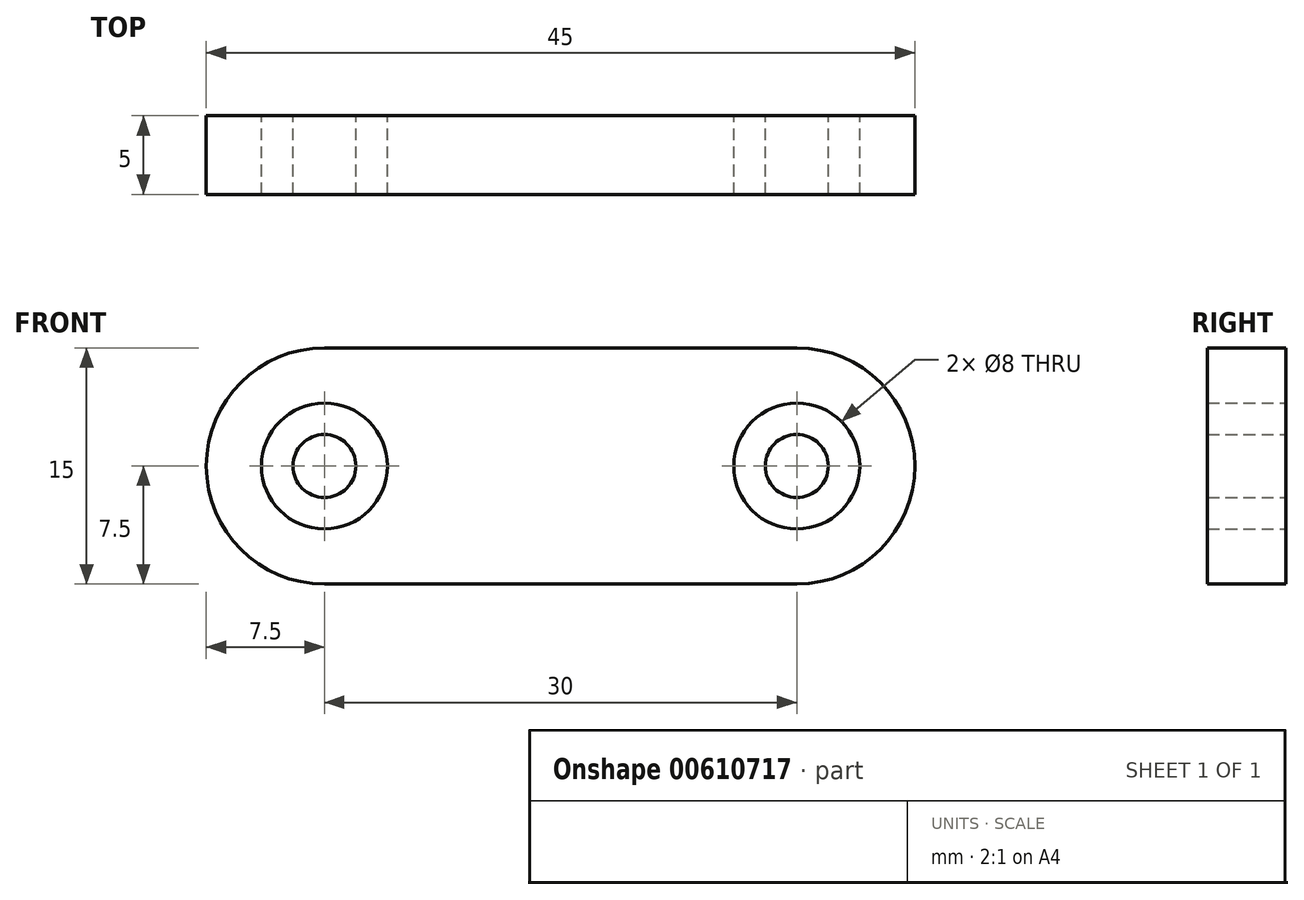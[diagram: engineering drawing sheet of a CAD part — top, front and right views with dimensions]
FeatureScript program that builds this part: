
annotation { "Feature Type Name" : "Feature", "Feature Type Description" : "" }
export const myFeature = defineFeature(function(context is Context, id is Id, definition is map)
    precondition{}
    {
        {
            var Q0;
            Q0=qCreatedBy(makeId("Front.planeOp"),FACE);
            var sketch = newSketch(context, id + "F0", { "sketchPlane" : qUnion([Q0])});
            skArc(sketch, "E0", {"start": v(0, 7.5) * mm, "mid": v(-7.5, 0) * mm, "end": v(0, -7.5) * mm});
            skArc(sketch, "E1", {"start": v(30, -7.5) * mm, "mid": v(37.5, 0) * mm, "end": v(30, 7.5) * mm});
            skLineSegment(sketch, "E2", {"start": v(0, 7.5) * mm, "end": v(30, 7.5) * mm});
            skLineSegment(sketch, "E3", {"start": v(0, -7.5) * mm, "end": v(30, -7.5) * mm});
            skCircle(sketch, "E4", {"center": v(0, 0) * mm, "radius": 4 * mm});
            skCircle(sketch, "E5", {"center": v(30, 0) * mm, "radius": 4 * mm});
            skSolve(sketch);
        }
        {
            var Q0;
            Q0 = qSketchRegion(id + "F0", true);
            extrude(context, id + "F1", {"entities" : qUnion([Q0]), "depth" : 5 * mm, "offsetDistance" : 25.4 * mm});
        }
        {
            var Q0;
            Q0=qCreatedBy(makeId("Front.planeOp"),FACE);
            var sketch = newSketch(context, id + "F2", { "sketchPlane" : qUnion([Q0])});
            skCircle(sketch, "E6", {"center": v(0, 0) * mm, "radius": 2 * mm});
            skLineSegment(sketch, "E7", {"start": v(30, 10.11) * mm, "end": v(30, -12.1) * mm, "construction": true});
            skCircle(sketch, "E8", {"center": v(30, 0) * mm, "radius": 2 * mm});
            skSolve(sketch);
        }
        {
            var Q0;
            Q0 = qSketchRegion(id + "F2", true);
            extrude(context, id + "F3", {"entities" : qUnion([Q0]), "depth" : 5 * mm, "offsetDistance" : 25.4 * mm});
        }
    });
